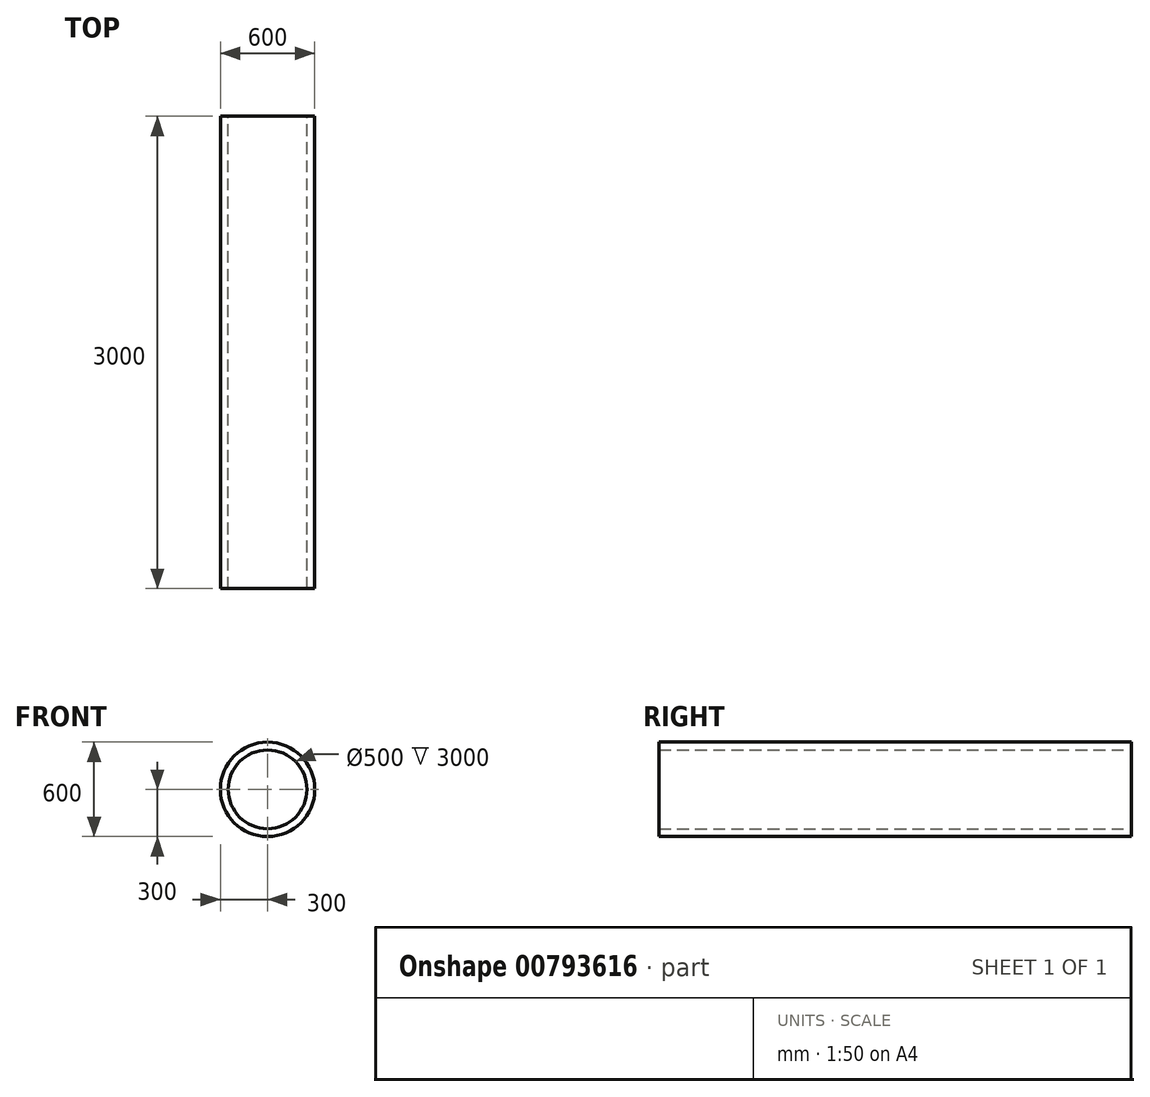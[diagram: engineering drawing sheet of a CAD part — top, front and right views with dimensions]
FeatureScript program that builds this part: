
annotation { "Feature Type Name" : "Feature", "Feature Type Description" : "" }
export const myFeature = defineFeature(function(context is Context, id is Id, definition is map)
    precondition{}
    {
        {
            var Q0;
            Q0=qCreatedBy(makeId("Front.planeOp"),FACE);
            var sketch = newSketch(context, id + "F0", { "sketchPlane" : qUnion([Q0])});
            skCircle(sketch, "E0", {"center": v(0, 0) * mm, "radius": 250 * mm});
            skCircle(sketch, "E1", {"center": v(0, 0) * mm, "radius": 300 * mm});
            skSolve(sketch);
        }
        {
            var Q0;
            Q0=makeQuery(id+"F0.imprint","IMPRINT",FACE,{"disambiguationData":[TD([[makeQuery(id+"F0.imprint","IMPRINT",EDGE,{"derivedFrom":sQuery(id+"F0.wireOp",EDGE,"E0")}),-1.0]])]});
            extrude(context, id + "F1", {"entities" : qUnion([Q0]), "endBound" : BoundingType.SYMMETRIC, "depth" : 3000 * mm, "offsetDistance" : 25 * mm});
        }
    });
